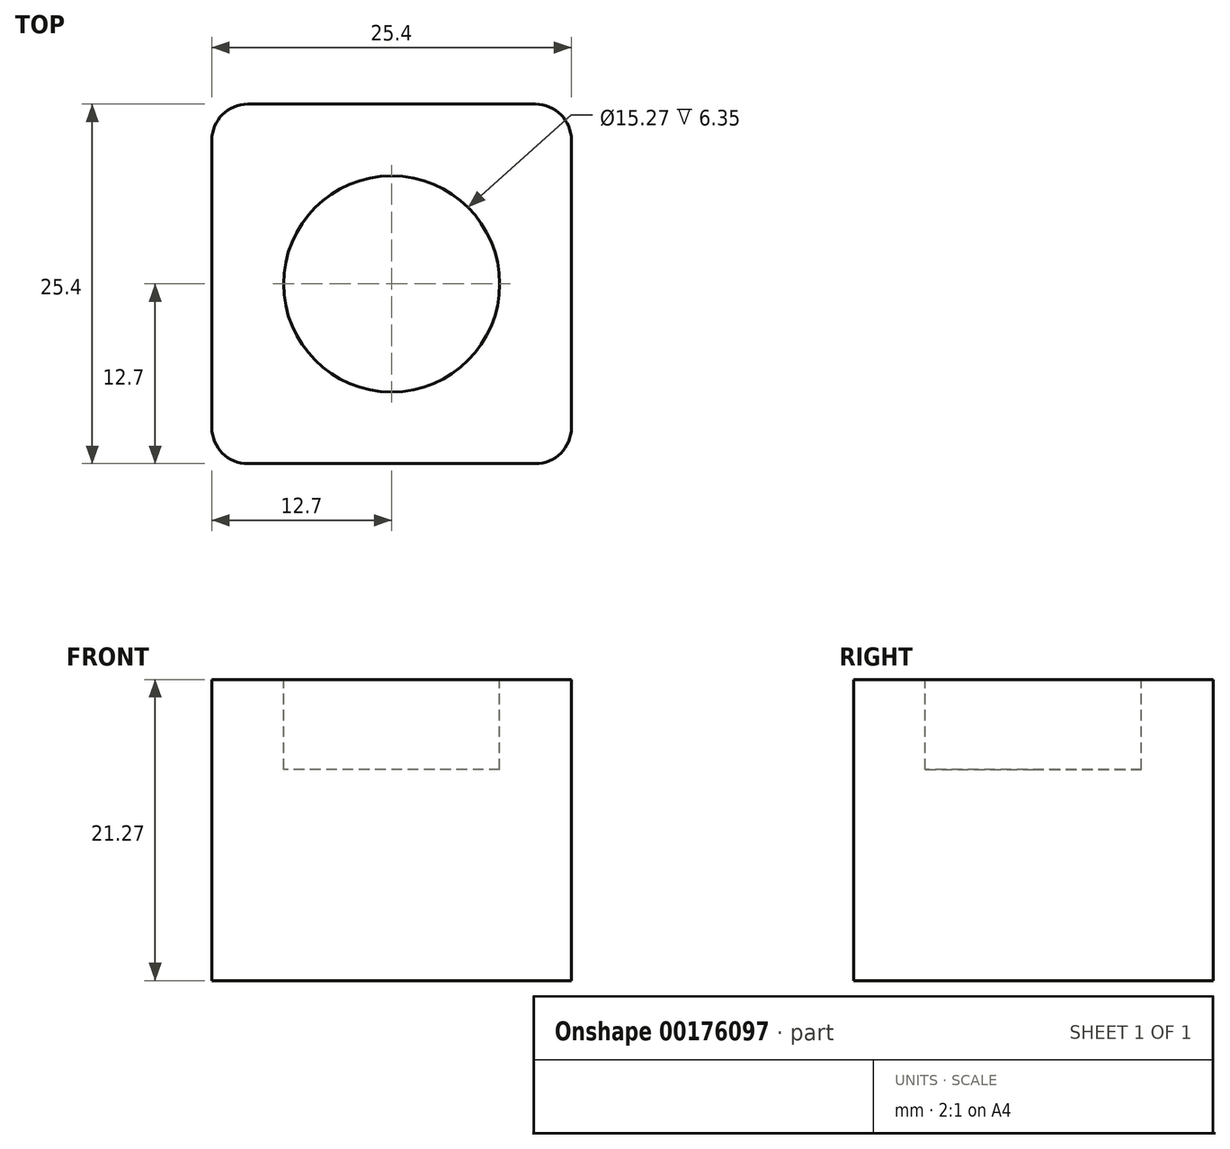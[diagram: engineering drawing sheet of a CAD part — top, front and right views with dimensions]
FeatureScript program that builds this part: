
annotation { "Feature Type Name" : "Feature", "Feature Type Description" : "" }
export const myFeature = defineFeature(function(context is Context, id is Id, definition is map)
    precondition{}
    {
        {
            var Q0;
            Q0=qCreatedBy(makeId("Top.planeOp"),FACE);
            var sketch = newSketch(context, id + "F0", { "sketchPlane" : qUnion([Q0])});
            skLineSegment(sketch, "E0.bottom", {"start": v(-10.16, 12.7) * mm, "end": v(10.16, 12.7) * mm});
            skLineSegment(sketch, "E0.top", {"start": v(-10.16, -12.7) * mm, "end": v(10.16, -12.7) * mm});
            skLineSegment(sketch, "E0.left", {"start": v(-12.7, 10.16) * mm, "end": v(-12.7, -10.16) * mm});
            skLineSegment(sketch, "E0.right", {"start": v(12.7, 10.16) * mm, "end": v(12.7, -10.16) * mm});
            skPoint(sketch, "E1.visualSharp", {"position": v(-12.7, 12.7) * mm});
            skArc(sketch, "E1.filletArc", {"start": v(-10.16, 12.7) * mm, "mid": v(-11.96, 11.96) * mm, "end": v(-12.7, 10.16) * mm});
            skPoint(sketch, "E2.visualSharp", {"position": v(12.7, 12.7) * mm});
            skArc(sketch, "E2.filletArc", {"start": v(12.7, 10.16) * mm, "mid": v(11.96, 11.96) * mm, "end": v(10.16, 12.7) * mm});
            skPoint(sketch, "E3.visualSharp", {"position": v(12.7, -12.7) * mm});
            skArc(sketch, "E3.filletArc", {"start": v(10.16, -12.7) * mm, "mid": v(11.96, -11.96) * mm, "end": v(12.7, -10.16) * mm});
            skPoint(sketch, "E4.visualSharp", {"position": v(-12.7, -12.7) * mm});
            skArc(sketch, "E4.filletArc", {"start": v(-12.7, -10.16) * mm, "mid": v(-11.96, -11.96) * mm, "end": v(-10.16, -12.7) * mm});
            skSolve(sketch);
        }
        {
            var Q0;
            Q0=makeQuery(id+"F0.imprint","IMPRINT",FACE,{"disambiguationData":[TD([[makeQuery(id+"F0.imprint","IMPRINT",EDGE,{"derivedFrom":sQuery(id+"F0.wireOp",EDGE,"E0.bottom")}),-1.0]])]});
            extrude(context, id + "F1", {"entities" : qUnion([Q0]), "depth" : 21.27 * mm});
        }
        {
            var Q0;
            Q0=makeQuery(id+"F1.opExtrude","CAP_FACE",FACE,{"disambiguationData":[OSD([sQuery(id+"F0.wireOp",EDGE,"E0.bottom"),sQuery(id+"F0.wireOp",EDGE,"E0.top"),sQuery(id+"F0.wireOp",EDGE,"E0.left"),sQuery(id+"F0.wireOp",EDGE,"E0.right"),sQuery(id+"F0.wireOp",EDGE,"E1.filletArc"),sQuery(id+"F0.wireOp",EDGE,"E2.filletArc"),sQuery(id+"F0.wireOp",EDGE,"E3.filletArc"),sQuery(id+"F0.wireOp",EDGE,"E4.filletArc")])],"isStart":false});
            var sketch = newSketch(context, id + "F2", { "sketchPlane" : qUnion([Q0])});
            skCircle(sketch, "E5", {"center": v(0, 0) * mm, "radius": 7.63 * mm});
            skSolve(sketch);
        }
        {
            var Q0;
            Q0 = qSketchRegion(id + "F2", true);
            var Q1;
            Q1=makeQuery(id+"F2.imprint","IMPRINT",FACE,{"disambiguationData":[TD([[makeQuery(id+"F2.imprint","IMPRINT",EDGE,{"derivedFrom":sQuery(id+"F2.wireOp",EDGE,"E5")}),1.0]])]});
            extrude(context, id + "F3", {"entities" : qUnion([Q0, Q1]), "operationType" : NewBodyOperationType.REMOVE, "oppositeDirection" : true, "depth" : 6.35 * mm});
        }
    });
